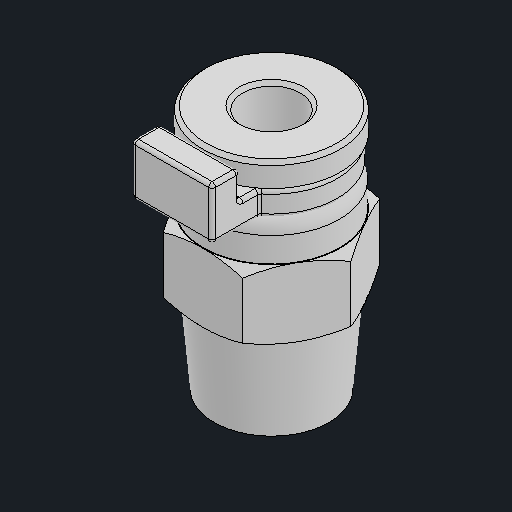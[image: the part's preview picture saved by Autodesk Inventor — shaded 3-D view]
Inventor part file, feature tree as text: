
AUTODESK INVENTOR PART (.ipt)
format: ipt  version: 2024.2 (Build 282272000, 272)  size: 227,840 bytes
history: native  units: mm
features: other x4, chamfer x1, fillet x1
ambient origin geometry x8: Origin, YZ Plane, XZ Plane, XY Plane, X Axis, Y Axis, Z Axis, Center Point
bodies: Body1 (feature_tree), Body2 (feature_tree), Body3 (feature_tree)
feature tree (6):
  other  "솔리드1"
  other  "솔리드2"
  other  "솔리드3"
  other  "Cut-Extrude5[1]"
  chamfer  "Chamfer1"  [1 undecoded]
  fillet  "Fillet2"  [1 undecoded]
note: 2 required parameter values undecoded (feature->parameter linkage not recoverable at this tier; creation-order binding heuristic only, values carry confidence <= 0.55)
